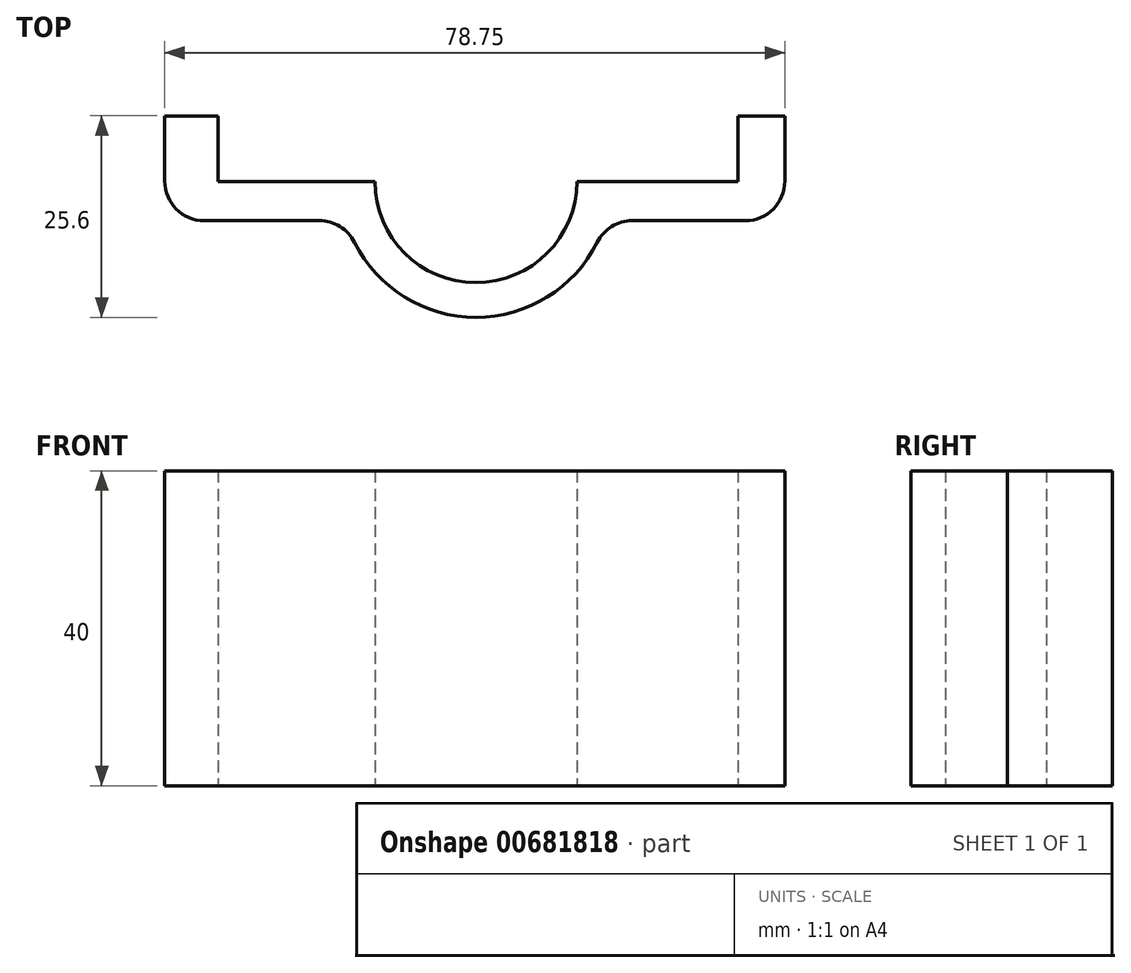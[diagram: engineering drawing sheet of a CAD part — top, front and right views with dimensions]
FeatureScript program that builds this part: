
annotation { "Feature Type Name" : "Feature", "Feature Type Description" : "" }
export const myFeature = defineFeature(function(context is Context, id is Id, definition is map)
    precondition{}
    {
        {
            var Q0;
            Q0=qCreatedBy(makeId("Top.planeOp"),FACE);
            var sketch = newSketch(context, id + "F0", { "sketchPlane" : qUnion([Q0])});
            skArc(sketch, "E0", {"start": v(-12.82, 0) * mm, "mid": v(0, -12.82) * mm, "end": v(12.82, 0) * mm});
            skLineSegment(sketch, "E1", {"start": v(12.82, 0) * mm, "end": v(33.28, 0) * mm});
            skLineSegment(sketch, "E2", {"start": v(33.28, 0) * mm, "end": v(33.28, 8.36) * mm});
            skLineSegment(sketch, "E3", {"start": v(33.28, 8.36) * mm, "end": v(39.23, 8.36) * mm});
            skLineSegment(sketch, "E4", {"start": v(39.23, 8.36) * mm, "end": v(39.23, -4.96) * mm});
            skLineSegment(sketch, "E5", {"start": v(39.23, -4.96) * mm, "end": v(16.5, -4.96) * mm});
            skLineSegment(sketch, "E6", {"start": v(-16.5, -4.96) * mm, "end": v(-39.52, -4.96) * mm});
            skLineSegment(sketch, "E7", {"start": v(-39.52, -4.96) * mm, "end": v(-39.52, 8.36) * mm});
            skLineSegment(sketch, "E8", {"start": v(-39.52, 8.36) * mm, "end": v(-32.72, 8.36) * mm});
            skLineSegment(sketch, "E9", {"start": v(-32.72, 8.36) * mm, "end": v(-32.72, 0) * mm});
            skLineSegment(sketch, "E10", {"start": v(-32.72, 0) * mm, "end": v(-11.82, 0) * mm});
            skArc(sketch, "E11", {"start": v(-16.5, -4.96) * mm, "mid": v(0, -17.24) * mm, "end": v(16.5, -4.96) * mm});
            skPoint(sketch, "E12.orphan", {"position": v(-11.82, -4.96) * mm});
            skSolve(sketch);
        }
        {
            var Q0;
            {var subQ1=sQuery(id+"F0.wireOp",EDGE,"E0");Q0=makeQuery(id+"F0.imprint","IMPRINT",FACE,{"disambiguationData":[TD([[makeQuery(id+"F0.imprint","IMPRINT",EDGE,{"derivedFrom":subQ1}),-1.0]])]});}
            extrude(context, id + "F1", {"entities" : qUnion([Q0]), "depth" : 40 * mm, "offsetDistance" : 25 * mm});
        }
        {
            var Q0;
            Q0=makeQuery(id+"F1.opExtrude","SWEPT_EDGE",EDGE,{"disambiguationData":[OSD([sQuery(id+"F0.wireOp",EDGE,"E5"),sQuery(id+"F0.wireOp",EDGE,"E11")])]});
            var Q1;
            Q1=makeQuery(id+"F1.opExtrude","SWEPT_EDGE",EDGE,{"disambiguationData":[OSD([sQuery(id+"F0.wireOp",EDGE,"E4"),sQuery(id+"F0.wireOp",EDGE,"E5")])]});
            var Q2;
            Q2=makeQuery(id+"F1.opExtrude","SWEPT_EDGE",EDGE,{"disambiguationData":[OSD([sQuery(id+"F0.wireOp",EDGE,"E6"),sQuery(id+"F0.wireOp",EDGE,"E7")])]});
            var Q3;
            Q3=makeQuery(id+"F1.opExtrude","SWEPT_EDGE",EDGE,{"disambiguationData":[OSD([sQuery(id+"F0.wireOp",EDGE,"E6"),sQuery(id+"F0.wireOp",EDGE,"E11")])]});
            fillet(context, id + "F2", {"entities" : qUnion([Q0, Q1, Q2, Q3]), "radius" : 5 * mm, "tangentPropagation" : true, "allowEdgeOverflow" : false});
        }
    });
